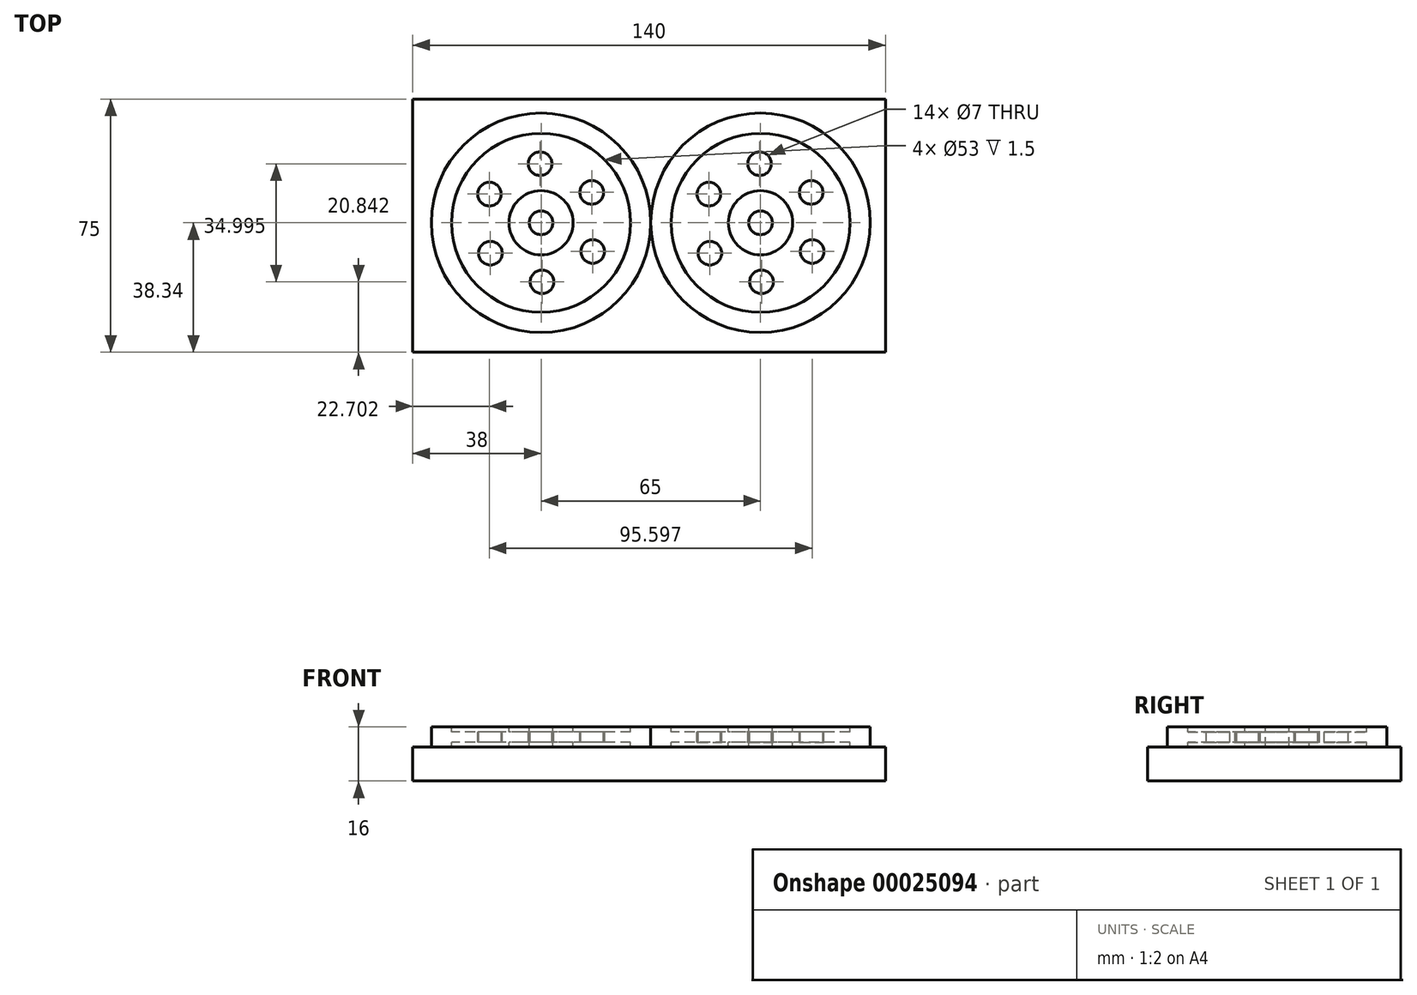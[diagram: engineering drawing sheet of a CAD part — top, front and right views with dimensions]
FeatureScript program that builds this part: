
annotation { "Feature Type Name" : "Feature", "Feature Type Description" : "" }
export const myFeature = defineFeature(function(context is Context, id is Id, definition is map)
    precondition{}
    {
        {
            var Q0;
            Q0=qCreatedBy(makeId("Front.planeOp"),FACE);
            var sketch = newSketch(context, id + "F0", { "sketchPlane" : qUnion([Q0])});
            skLineSegment(sketch, "E0", {"start": v(-32.5, 54.8) * mm, "end": v(-32.5, -51.85) * mm, "construction": true});
            skLineSegment(sketch, "E1", {"start": v(32.5, 54.8) * mm, "end": v(32.5, -51.85) * mm, "construction": true});
            skLineSegment(sketch, "E2.bottom", {"start": v(-29, 6) * mm, "end": v(-23, 6) * mm});
            skLineSegment(sketch, "E2.top", {"start": v(-29, 0) * mm, "end": v(-23, 0) * mm});
            skLineSegment(sketch, "E2.left", {"start": v(-29, 6) * mm, "end": v(-29, 0) * mm});
            skLineSegment(sketch, "E2.right", {"start": v(-23, 6) * mm, "end": v(-23, 4.5) * mm});
            skLineSegment(sketch, "E3.bottom", {"start": v(-23, 4.5) * mm, "end": v(-6, 4.5) * mm});
            skLineSegment(sketch, "E3.top", {"start": v(-23, 1.5) * mm, "end": v(-6, 1.5) * mm});
            skLineSegment(sketch, "E4.bottom", {"start": v(-6, 6) * mm, "end": v(0, 6) * mm});
            skLineSegment(sketch, "E4.top", {"start": v(-6, 0) * mm, "end": v(0, 0) * mm});
            skLineSegment(sketch, "E4.left", {"start": v(-6, 6) * mm, "end": v(-6, 4.5) * mm});
            skLineSegment(sketch, "E4.right", {"start": v(0, 6) * mm, "end": v(0, 0) * mm});
            skLineSegment(sketch, "E5.bottom", {"start": v(0, 6) * mm, "end": v(6, 6) * mm});
            skLineSegment(sketch, "E5.top", {"start": v(0, 0) * mm, "end": v(6, 0) * mm});
            skLineSegment(sketch, "E5.right", {"start": v(6, 6) * mm, "end": v(6, 4.5) * mm});
            skLineSegment(sketch, "E6.bottom", {"start": v(6, 4.5) * mm, "end": v(23, 4.5) * mm});
            skLineSegment(sketch, "E6.top", {"start": v(6, 1.5) * mm, "end": v(23, 1.5) * mm});
            skLineSegment(sketch, "E7.bottom", {"start": v(23, 6) * mm, "end": v(29, 6) * mm});
            skLineSegment(sketch, "E7.top", {"start": v(23, 0) * mm, "end": v(29, 0) * mm});
            skLineSegment(sketch, "E7.left", {"start": v(23, 6) * mm, "end": v(23, 4.5) * mm});
            skLineSegment(sketch, "E7.right", {"start": v(29, 6) * mm, "end": v(29, 0) * mm});
            skLineSegment(sketch, "E8.trimOffspring", {"start": v(-23, 1.5) * mm, "end": v(-23, 0) * mm});
            skLineSegment(sketch, "E9.trimOffspring", {"start": v(-6, 1.5) * mm, "end": v(-6, 0) * mm});
            skLineSegment(sketch, "E10.trimOffspring", {"start": v(6, 1.5) * mm, "end": v(6, 0) * mm});
            skLineSegment(sketch, "E11.trimOffspring", {"start": v(23, 1.5) * mm, "end": v(23, 0) * mm});
            skSolve(sketch);
        }
        {
            var Q0;
            Q0=makeQuery(id+"F0.imprint","IMPRINT",FACE,{"disambiguationData":[TD([[makeQuery(id+"F0.imprint","IMPRINT",EDGE,{"derivedFrom":sQuery(id+"F0.wireOp",EDGE,"E5.bottom")}),-1.0]])]});
            var Q1;
            Q1=sQuery(id+"F0.wireOp",EDGE,"E1");
            revolve(context, id + "F1", {"entities" : qUnion([Q0]), "axis" : qUnion([Q1]), "revolveType" : RevolveType.FULL});
        }
        {
            var Q0;
            Q0=makeQuery(id+"F0.imprint","IMPRINT",FACE,{"disambiguationData":[TD([[makeQuery(id+"F0.imprint","IMPRINT",EDGE,{"derivedFrom":sQuery(id+"F0.wireOp",EDGE,"E2.bottom")}),-1.0]])]});
            var Q1;
            Q1=sQuery(id+"F0.wireOp",EDGE,"E0");
            revolve(context, id + "F2", {"entities" : qUnion([Q0]), "axis" : qUnion([Q1]), "revolveType" : RevolveType.FULL});
        }
        {
            var Q0;
            Q0=makeQuery(id+"F2.opRevolve","SWEPT_FACE",FACE,{"disambiguationData":[OSD([sQuery(id+"F0.wireOp",EDGE,"E3.bottom")])]});
            var sketch = newSketch(context, id + "F3", { "sketchPlane" : qUnion([Q0])});
            skCircle(sketch, "E12", {"center": v(-32.8, 17.5) * mm, "radius": 3.5 * mm});
            skCircle(sketch, "E13.1.0", {"center": v(-17.5, 9) * mm, "radius": 3.5 * mm});
            skCircle(sketch, "E13.2.0", {"center": v(-17.2, -8.5) * mm, "radius": 3.5 * mm});
            skCircle(sketch, "E13.3.0", {"center": v(-32.2, -17.5) * mm, "radius": 3.5 * mm});
            skCircle(sketch, "E13.4.0", {"center": v(-47.5, -9) * mm, "radius": 3.5 * mm});
            skCircle(sketch, "E13.5.0", {"center": v(-47.8, 8.5) * mm, "radius": 3.5 * mm});
            skPoint(sketch, "E13.center", {"position": v(-32.5, 0) * mm});
            skLineSegment(sketch, "E13.anchor1", {"start": v(-32.5, 0) * mm, "end": v(-32.8, 17.5) * mm, "construction": true});
            skLineSegment(sketch, "E13.anchor2", {"start": v(-32.5, 0) * mm, "end": v(-47.8, 8.5) * mm, "construction": true});
            skSolve(sketch);
        }
        {
            var Q0;
            Q0=makeQuery(id+"F3.imprint","IMPRINT",FACE,{"disambiguationData":[TD([[makeQuery(id+"F3.imprint","IMPRINT",EDGE,{"derivedFrom":sQuery(id+"F3.wireOp",EDGE,"E13.2.0")}),1.0]])]});
            var Q1;
            Q1=makeQuery(id+"F3.imprint","IMPRINT",FACE,{"disambiguationData":[TD([[makeQuery(id+"F3.imprint","IMPRINT",EDGE,{"derivedFrom":sQuery(id+"F3.wireOp",EDGE,"E13.3.0")}),1.0]])]});
            var Q2;
            Q2=makeQuery(id+"F3.imprint","IMPRINT",FACE,{"disambiguationData":[TD([[makeQuery(id+"F3.imprint","IMPRINT",EDGE,{"derivedFrom":sQuery(id+"F3.wireOp",EDGE,"E13.4.0")}),1.0]])]});
            var Q3;
            Q3=makeQuery(id+"F3.imprint","IMPRINT",FACE,{"disambiguationData":[TD([[makeQuery(id+"F3.imprint","IMPRINT",EDGE,{"derivedFrom":sQuery(id+"F3.wireOp",EDGE,"E13.5.0")}),1.0]])]});
            var Q4;
            Q4=makeQuery(id+"F3.imprint","IMPRINT",FACE,{"disambiguationData":[TD([[makeQuery(id+"F3.imprint","IMPRINT",EDGE,{"derivedFrom":sQuery(id+"F3.wireOp",EDGE,"E13.1.0")}),1.0]])]});
            var Q5;
            Q5=makeQuery(id+"F3.imprint","IMPRINT",FACE,{"disambiguationData":[TD([[makeQuery(id+"F3.imprint","IMPRINT",EDGE,{"derivedFrom":sQuery(id+"F3.wireOp",EDGE,"E12")}),1.0]])]});
            extrude(context, id + "F4", {"entities" : qUnion([Q0, Q1, Q2, Q3, Q4, Q5]), "operationType" : NewBodyOperationType.REMOVE, "endBound" : BoundingType.THROUGH_ALL, "oppositeDirection" : true, "depth" : 25 * mm});
        }
        {
            var Q0;
            Q0=makeQuery(id+"F1.opRevolve","SWEPT_FACE",FACE,{"disambiguationData":[OSD([sQuery(id+"F0.wireOp",EDGE,"E6.bottom")])]});
            var sketch = newSketch(context, id + "F5", { "sketchPlane" : qUnion([Q0])});
            skCircle(sketch, "E14", {"center": v(47.5, 9) * mm, "radius": 3.5 * mm});
            skCircle(sketch, "E15.1.0", {"center": v(32.2, 17.5) * mm, "radius": 3.5 * mm});
            skCircle(sketch, "E15.2.0", {"center": v(17.2, 8.5) * mm, "radius": 3.5 * mm});
            skCircle(sketch, "E15.3.0", {"center": v(17.5, -9) * mm, "radius": 3.5 * mm});
            skCircle(sketch, "E15.4.0", {"center": v(32.8, -17.5) * mm, "radius": 3.5 * mm});
            skCircle(sketch, "E15.5.0", {"center": v(47.8, -8.5) * mm, "radius": 3.5 * mm});
            skPoint(sketch, "E15.center", {"position": v(32.5, 0) * mm});
            skSolve(sketch);
        }
        {
            var Q0;
            Q0 = qSketchRegion(id + "F5", true);
            extrude(context, id + "F6", {"entities" : qUnion([Q0]), "operationType" : NewBodyOperationType.REMOVE, "endBound" : BoundingType.THROUGH_ALL, "oppositeDirection" : true, "depth" : 25 * mm});
        }
        {
            var Q0;
            Q0=qCreatedBy(makeId("Top.planeOp"),FACE);
            var sketch = newSketch(context, id + "F7", { "sketchPlane" : qUnion([Q0])});
            skLineSegment(sketch, "E16.bottom", {"start": v(-70.5, 36.66) * mm, "end": v(69.5, 36.66) * mm});
            skLineSegment(sketch, "E16.top", {"start": v(-70.5, -38.34) * mm, "end": v(69.5, -38.34) * mm});
            skLineSegment(sketch, "E16.left", {"start": v(-70.5, 36.66) * mm, "end": v(-70.5, -38.34) * mm});
            skLineSegment(sketch, "E16.right", {"start": v(69.5, 36.66) * mm, "end": v(69.5, -38.34) * mm});
            skSolve(sketch);
        }
        {
            var Q0;
            Q0=makeQuery(id+"F7.imprint","IMPRINT",FACE,{"disambiguationData":[TD([[makeQuery(id+"F7.imprint","IMPRINT",EDGE,{"derivedFrom":sQuery(id+"F7.wireOp",EDGE,"E16.bottom")}),-1.0]])]});
            extrude(context, id + "F8", {"entities" : qUnion([Q0]), "oppositeDirection" : true, "depth" : 10 * mm});
        }
    });
